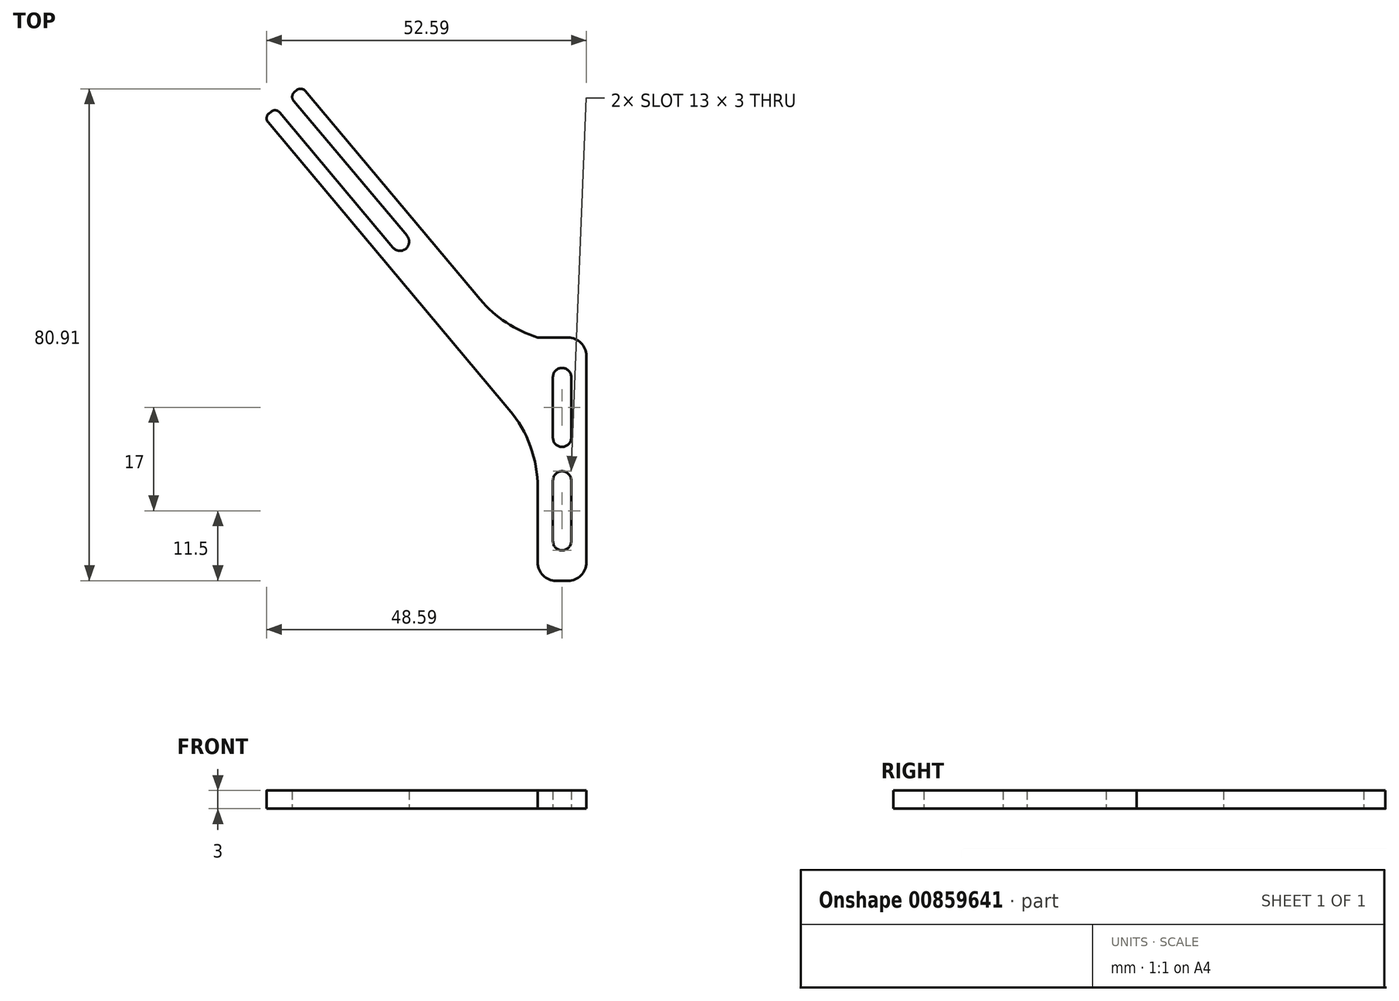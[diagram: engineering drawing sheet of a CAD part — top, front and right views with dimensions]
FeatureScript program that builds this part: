
annotation { "Feature Type Name" : "Feature", "Feature Type Description" : "" }
export const myFeature = defineFeature(function(context is Context, id is Id, definition is map)
    precondition{}
    {
        {
            var Q0;
            Q0=qCreatedBy(makeId("Top.planeOp"),FACE);
            var sketch = newSketch(context, id + "F0", { "sketchPlane" : qUnion([Q0])});
            skLineSegment(sketch, "E0", {"start": v(-8, 35) * mm, "end": v(-8, 92.89) * mm, "construction": true});
            skCircle(sketch, "E1", {"center": v(-4, 28.5) * mm, "radius": 1.5 * mm, "construction": true});
            skCircle(sketch, "E2", {"center": v(-4, 11.5) * mm, "radius": 1.5 * mm, "construction": true});
            skLineSegment(sketch, "E3.bottom", {"start": v(-2.5, 23.5) * mm, "end": v(-5.5, 23.5) * mm, "construction": true});
            skLineSegment(sketch, "E3.top", {"start": v(-2.5, 33.5) * mm, "end": v(-5.5, 33.5) * mm, "construction": true});
            skLineSegment(sketch, "E3.left", {"start": v(-2.5, 23.5) * mm, "end": v(-2.5, 33.5) * mm});
            skLineSegment(sketch, "E3.right", {"start": v(-5.5, 23.5) * mm, "end": v(-5.5, 33.5) * mm});
            skLineSegment(sketch, "E4.bottom", {"start": v(-2.5, 6.5) * mm, "end": v(-5.5, 6.5) * mm, "construction": true});
            skLineSegment(sketch, "E4.top", {"start": v(-2.5, 16.5) * mm, "end": v(-5.5, 16.5) * mm, "construction": true});
            skLineSegment(sketch, "E4.left", {"start": v(-2.5, 6.5) * mm, "end": v(-2.5, 16.5) * mm});
            skLineSegment(sketch, "E4.right", {"start": v(-5.5, 6.5) * mm, "end": v(-5.5, 16.5) * mm});
            skArc(sketch, "E5", {"start": v(-5.5, 33.5) * mm, "mid": v(-4, 35) * mm, "end": v(-2.5, 33.5) * mm});
            skArc(sketch, "E6", {"start": v(-5.5, 23.5) * mm, "mid": v(-4, 22) * mm, "end": v(-2.5, 23.5) * mm});
            skArc(sketch, "E7", {"start": v(-5.5, 16.5) * mm, "mid": v(-4, 18) * mm, "end": v(-2.5, 16.5) * mm});
            skArc(sketch, "E8", {"start": v(-5.5, 6.5) * mm, "mid": v(-4, 5) * mm, "end": v(-2.5, 6.5) * mm});
            skCircle(sketch, "E9", {"center": v(-30.65, 55.77) * mm, "radius": 1.5 * mm, "construction": true});
            skLineSegment(sketch, "E10", {"start": v(-30.65, 55.77) * mm, "end": v(-49.93, 78.75) * mm, "construction": true});
            skLineSegment(sketch, "E11", {"start": v(-31.8, 54.8) * mm, "end": v(-51.08, 77.78) * mm});
            skLineSegment(sketch, "E12", {"start": v(-29.5, 56.73) * mm, "end": v(-48.78, 79.71) * mm});
            skArc(sketch, "E13", {"start": v(-31.8, 54.8) * mm, "mid": v(-29.68, 54.62) * mm, "end": v(-29.5, 56.73) * mm});
            skPoint(sketch, "E14.visualSharp", {"position": v(-8, 0) * mm});
            skPoint(sketch, "E15.visualSharp", {"position": v(0, 0) * mm});
            skLineSegment(sketch, "E16", {"start": v(-8, 35) * mm, "end": v(-46.87, 81.32) * mm});
            skLineSegment(sketch, "E17", {"start": v(-8, -5) * mm, "end": v(-8, 22.55) * mm});
            skLineSegment(sketch, "E18", {"start": v(-8, 22.55) * mm, "end": v(-53, 76.18) * mm});
            skLineSegment(sketch, "E19", {"start": v(-51.08, 77.78) * mm, "end": v(-53, 76.18) * mm});
            skLineSegment(sketch, "E20", {"start": v(-48.78, 79.71) * mm, "end": v(-46.87, 81.32) * mm});
            skLineSegment(sketch, "E21", {"start": v(-51.08, 77.78) * mm, "end": v(-48.78, 79.71) * mm, "construction": true});
            skLineSegment(sketch, "E22", {"start": v(-8, 35) * mm, "end": v(-8, 40) * mm});
            skLineSegment(sketch, "E23", {"start": v(-8, 40) * mm, "end": v(0, 40) * mm});
            skLineSegment(sketch, "E24", {"start": v(0, 40) * mm, "end": v(0, 0) * mm});
            skLineSegment(sketch, "E25", {"start": v(0, 0) * mm, "end": v(-8, 0) * mm});
            skLineSegment(sketch, "E26", {"start": v(-4, 28.5) * mm, "end": v(-4, 40) * mm, "construction": true});
            skLineSegment(sketch, "E27", {"start": v(-4, 11.5) * mm, "end": v(-4, 0) * mm, "construction": true});
            skSolve(sketch);
        }
        {
            var Q0;
            Q0=makeQuery(id+"F0.imprint","IMPRINT",FACE,{"disambiguationData":[TD([[makeQuery(id+"F0.imprint","IMPRINT",EDGE,{"derivedFrom":sQuery(id+"F0.wireOp",EDGE,"E3.left")}),-1.0]])]});
            extrude(context, id + "F1", {"entities" : qUnion([Q0]), "depth" : 3 * mm, "offsetDistance" : 25 * mm});
        }
        {
            var Q0;
            Q0=makeQuery(id+"F1.opExtrude","SWEPT_EDGE",EDGE,{"disambiguationData":[OSD([sQuery(id+"F0.wireOp",EDGE,"E18"),sQuery(id+"F0.wireOp",EDGE,"E19")])]});
            var Q1;
            Q1=makeQuery(id+"F1.opExtrude","SWEPT_EDGE",EDGE,{"disambiguationData":[OSD([sQuery(id+"F0.wireOp",EDGE,"E11"),sQuery(id+"F0.wireOp",EDGE,"E19")])]});
            var Q2;
            Q2=makeQuery(id+"F1.opExtrude","SWEPT_EDGE",EDGE,{"disambiguationData":[OSD([sQuery(id+"F0.wireOp",EDGE,"E12"),sQuery(id+"F0.wireOp",EDGE,"E20")])]});
            var Q3;
            Q3=makeQuery(id+"F1.opExtrude","SWEPT_EDGE",EDGE,{"disambiguationData":[OSD([sQuery(id+"F0.wireOp",EDGE,"E16"),sQuery(id+"F0.wireOp",EDGE,"E20")])]});
            fillet(context, id + "F2", {"entities" : qUnion([Q0, Q1, Q2, Q3]), "radius" : 1 * mm, "tangentPropagation" : true, "allowEdgeOverflow" : false});
        }
        {
            var Q0;
            Q0=makeQuery(id+"F1.opExtrude","SWEPT_EDGE",EDGE,{"disambiguationData":[OSD([sQuery(id+"F0.wireOp",EDGE,"E16"),sQuery(id+"F0.wireOp",EDGE,"E22")])]});
            var Q1;
            Q1=makeQuery(id+"F1.opExtrude","SWEPT_EDGE",EDGE,{"disambiguationData":[OSD([sQuery(id+"F0.wireOp",EDGE,"E17"),sQuery(id+"F0.wireOp",EDGE,"E18")])]});
            fillet(context, id + "F3", {"entities" : qUnion([Q0, Q1]), "radius" : 20 * mm, "tangentPropagation" : true, "allowEdgeOverflow" : false});
        }
        {
            var Q0;
            Q0=makeQuery(id+"F1.opExtrude","SWEPT_EDGE",EDGE,{"disambiguationData":[OSD([sQuery(id+"F0.wireOp",EDGE,"E23"),sQuery(id+"F0.wireOp",EDGE,"E24")])]});
            var Q1;
            Q1=makeQuery(id+"F1.opExtrude","SWEPT_EDGE",EDGE,{"disambiguationData":[OSD([sQuery(id+"F0.wireOp",EDGE,"E17"),sQuery(id+"F0.wireOp",EDGE,"E25")])]});
            var Q2;
            Q2=makeQuery(id+"F1.opExtrude","SWEPT_EDGE",EDGE,{"disambiguationData":[OSD([sQuery(id+"F0.wireOp",EDGE,"E24"),sQuery(id+"F0.wireOp",EDGE,"E25")])]});
            fillet(context, id + "F4", {"entities" : qUnion([Q0, Q1, Q2]), "radius" : 3 * mm, "tangentPropagation" : true, "allowEdgeOverflow" : false});
        }
    });
